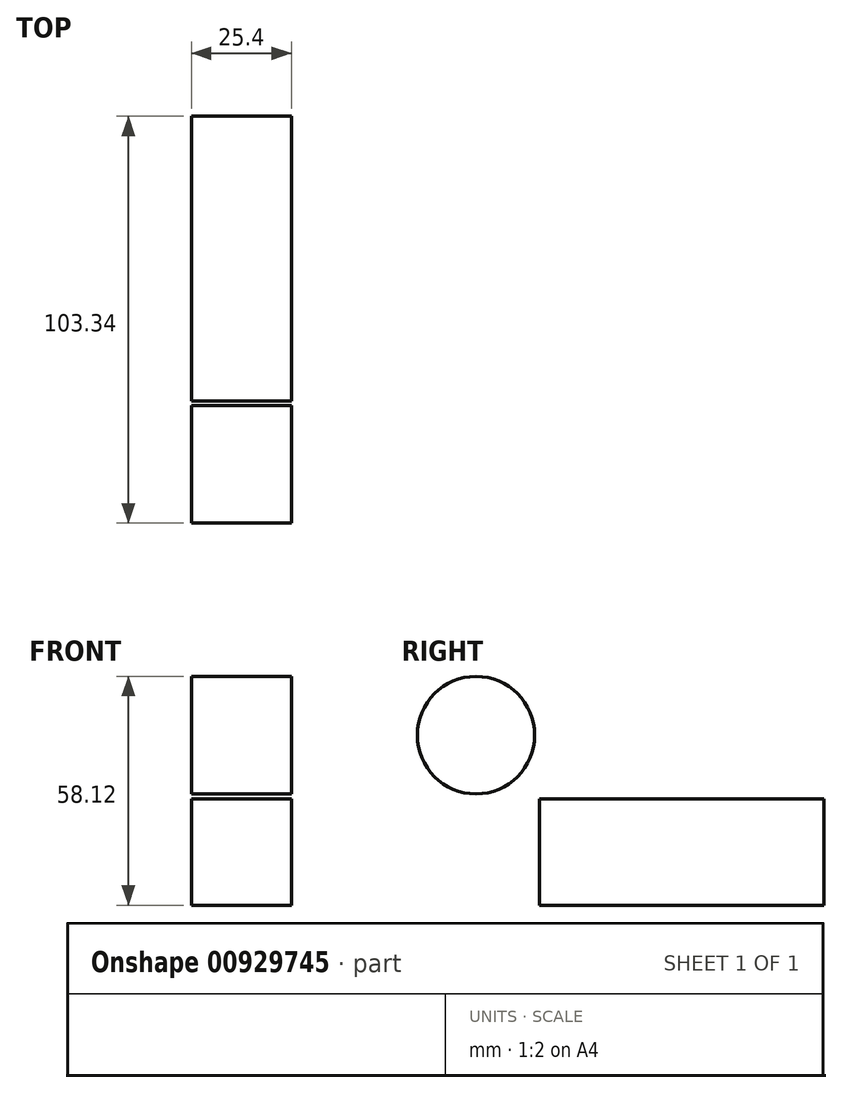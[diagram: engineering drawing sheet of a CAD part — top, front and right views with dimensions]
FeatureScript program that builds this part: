
annotation { "Feature Type Name" : "Feature", "Feature Type Description" : "" }
export const myFeature = defineFeature(function(context is Context, id is Id, definition is map)
    precondition{}
    {
        {
            var Q0;
            Q0=qCreatedBy(makeId("Right.planeOp"),FACE);
            var sketch = newSketch(context, id + "F0", { "sketchPlane" : qUnion([Q0])});
            skLineSegment(sketch, "E0.bottom", {"start": v(0, 27) * mm, "end": v(72.3, 27) * mm});
            skLineSegment(sketch, "E0.top", {"start": v(0, 0) * mm, "end": v(72.3, 0) * mm});
            skLineSegment(sketch, "E0.left", {"start": v(0, 27) * mm, "end": v(0, 0) * mm});
            skLineSegment(sketch, "E0.right", {"start": v(72.3, 27) * mm, "end": v(72.3, 0) * mm});
            skSolve(sketch);
        }
        {
            var Q0;
            Q0=makeQuery(id+"F0.imprint","IMPRINT",FACE,{"disambiguationData":[TD([[makeQuery(id+"F0.imprint","IMPRINT",EDGE,{"derivedFrom":sQuery(id+"F0.wireOp",EDGE,"E0.bottom")}),-1.0]])]});
            extrude(context, id + "F1", {"entities" : qUnion([Q0]), "depth" : 25.4 * mm, "offsetDistance" : 25.4 * mm});
        }
        {
            var Q0;
            Q0=qCreatedBy(makeId("Right.planeOp"),FACE);
            var sketch = newSketch(context, id + "F2", { "sketchPlane" : qUnion([Q0])});
            skCircle(sketch, "E1", {"center": v(-16.12, 43.2) * mm, "radius": 14.9 * mm});
            skSolve(sketch);
        }
        {
            var Q0;
            Q0=makeQuery(id+"F2.imprint","IMPRINT",FACE,{"disambiguationData":[TD([[makeQuery(id+"F2.imprint","IMPRINT",EDGE,{"derivedFrom":sQuery(id+"F2.wireOp",EDGE,"E1")}),1.0]])]});
            extrude(context, id + "F3", {"entities" : qUnion([Q0]), "depth" : 25.4 * mm, "offsetDistance" : 25.4 * mm});
        }
    });
